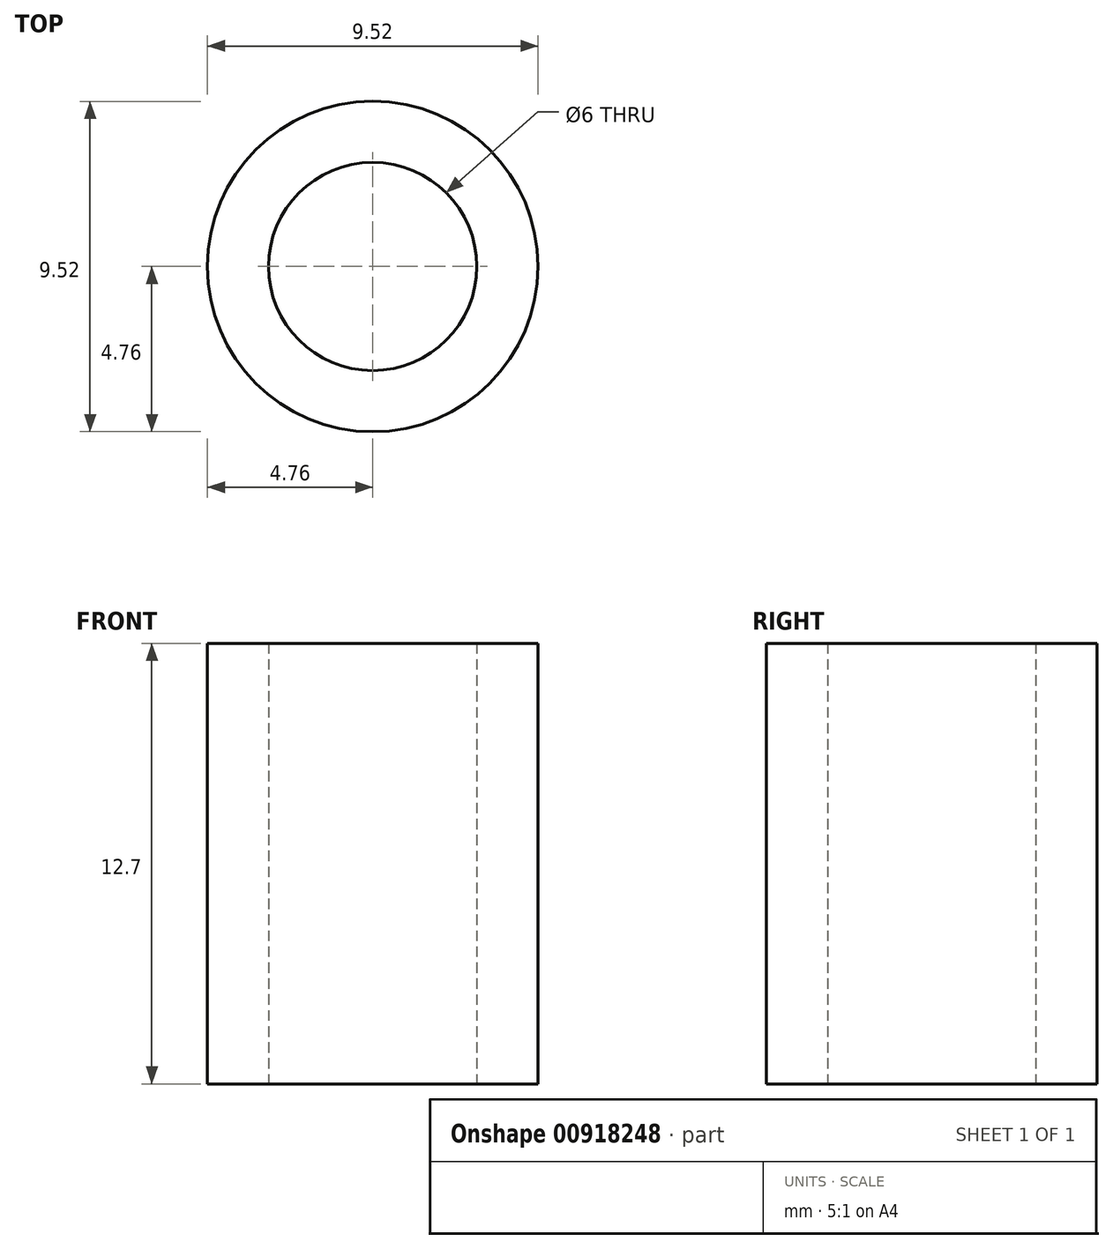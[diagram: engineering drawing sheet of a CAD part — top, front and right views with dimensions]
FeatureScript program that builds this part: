
annotation { "Feature Type Name" : "Feature", "Feature Type Description" : "" }
export const myFeature = defineFeature(function(context is Context, id is Id, definition is map)
    precondition{}
    {
        {
            var Q0;
            Q0=qCreatedBy(makeId("Top.planeOp"),FACE);
            var sketch = newSketch(context, id + "F0", { "sketchPlane" : qUnion([Q0])});
            skCircle(sketch, "E0", {"center": v(0, 0) * mm, "radius": 3 * mm});
            skCircle(sketch, "E1", {"center": v(0, 0) * mm, "radius": 4.76 * mm});
            skCircle(sketch, "E2", {"center": v(0, 0) * mm, "radius": 2.25 * mm, "construction": true});
            skSolve(sketch);
        }
        {
            var Q0;
            Q0 = qSketchRegion(id + "F0", true);
            extrude(context, id + "F1", {"entities" : qUnion([Q0]), "flatOperationType" : FlatOperationType.REMOVE, "depth" : 12.7 * mm, "offsetDistance" : 25 * mm, "domain" : OperationDomain.MODEL});
        }
    });
